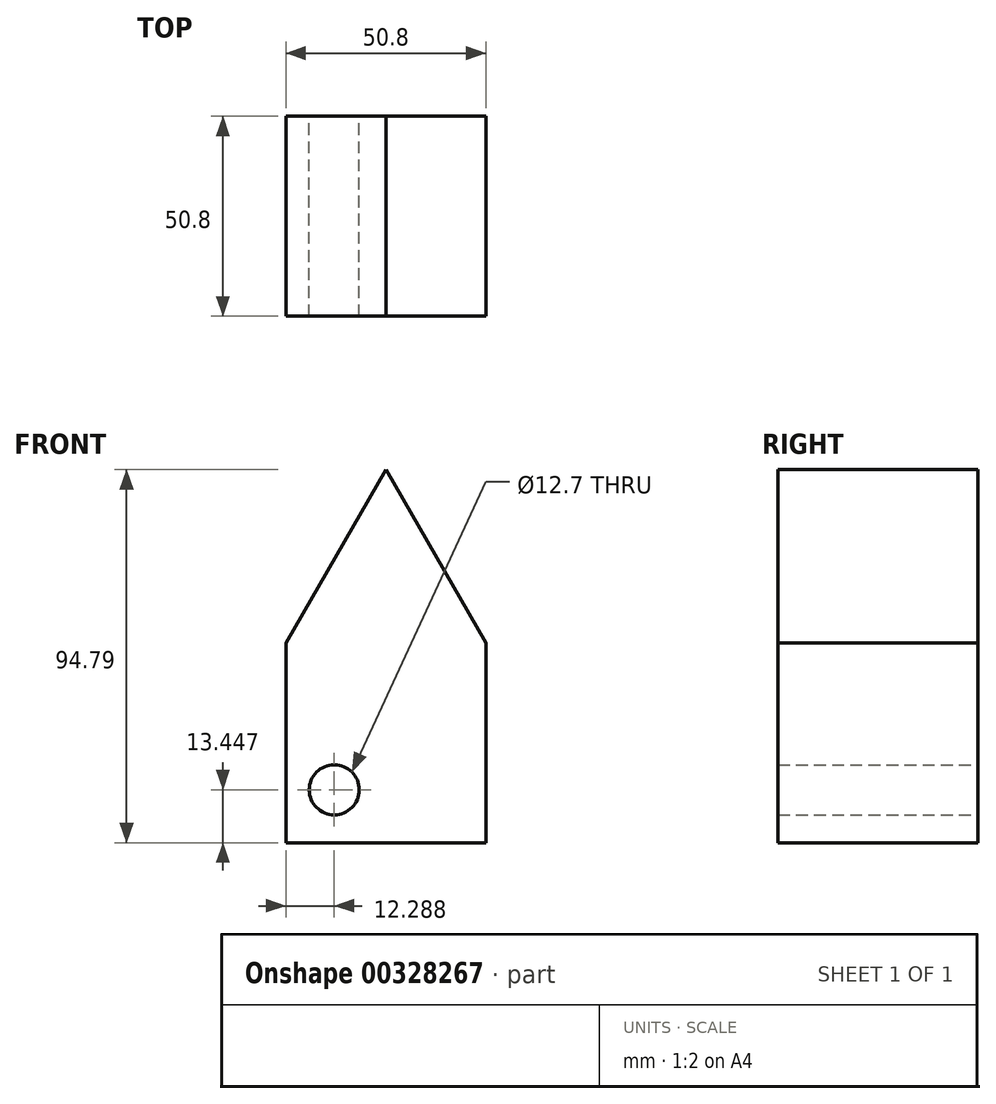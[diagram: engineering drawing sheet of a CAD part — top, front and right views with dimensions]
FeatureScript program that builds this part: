
annotation { "Feature Type Name" : "Feature", "Feature Type Description" : "" }
export const myFeature = defineFeature(function(context is Context, id is Id, definition is map)
    precondition{}
    {
        {
            var Q0;
            Q0=qCreatedBy(makeId("Front.planeOp"),FACE);
            var sketch = newSketch(context, id + "F0", { "sketchPlane" : qUnion([Q0])});
            skLineSegment(sketch, "E0.top", {"start": v(-25.4, -24.01) * mm, "end": v(25.4, -24.01) * mm});
            skLineSegment(sketch, "E0.left", {"start": v(-25.4, 26.79) * mm, "end": v(-25.4, -24.01) * mm});
            skLineSegment(sketch, "E0.right", {"start": v(25.4, 26.79) * mm, "end": v(25.4, -24.01) * mm});
            skLineSegment(sketch, "E1", {"start": v(-25.4, 26.79) * mm, "end": v(0, 70.78) * mm});
            skLineSegment(sketch, "E2", {"start": v(0, 70.78) * mm, "end": v(25.4, 26.79) * mm});
            skCircle(sketch, "E3", {"center": v(-13.11, -10.56) * mm, "radius": 6.35 * mm});
            skSolve(sketch);
        }
        {
            var Q0;
            Q0=makeQuery(id+"F0.imprint","IMPRINT",FACE,{"disambiguationData":[TD([[makeQuery(id+"F0.imprint","IMPRINT",EDGE,{"derivedFrom":sQuery(id+"F0.wireOp",EDGE,"E0.top")}),1.0]])]});
            extrude(context, id + "F1", {"entities" : qUnion([Q0]), "depth" : 50.8 * mm});
        }
    });
